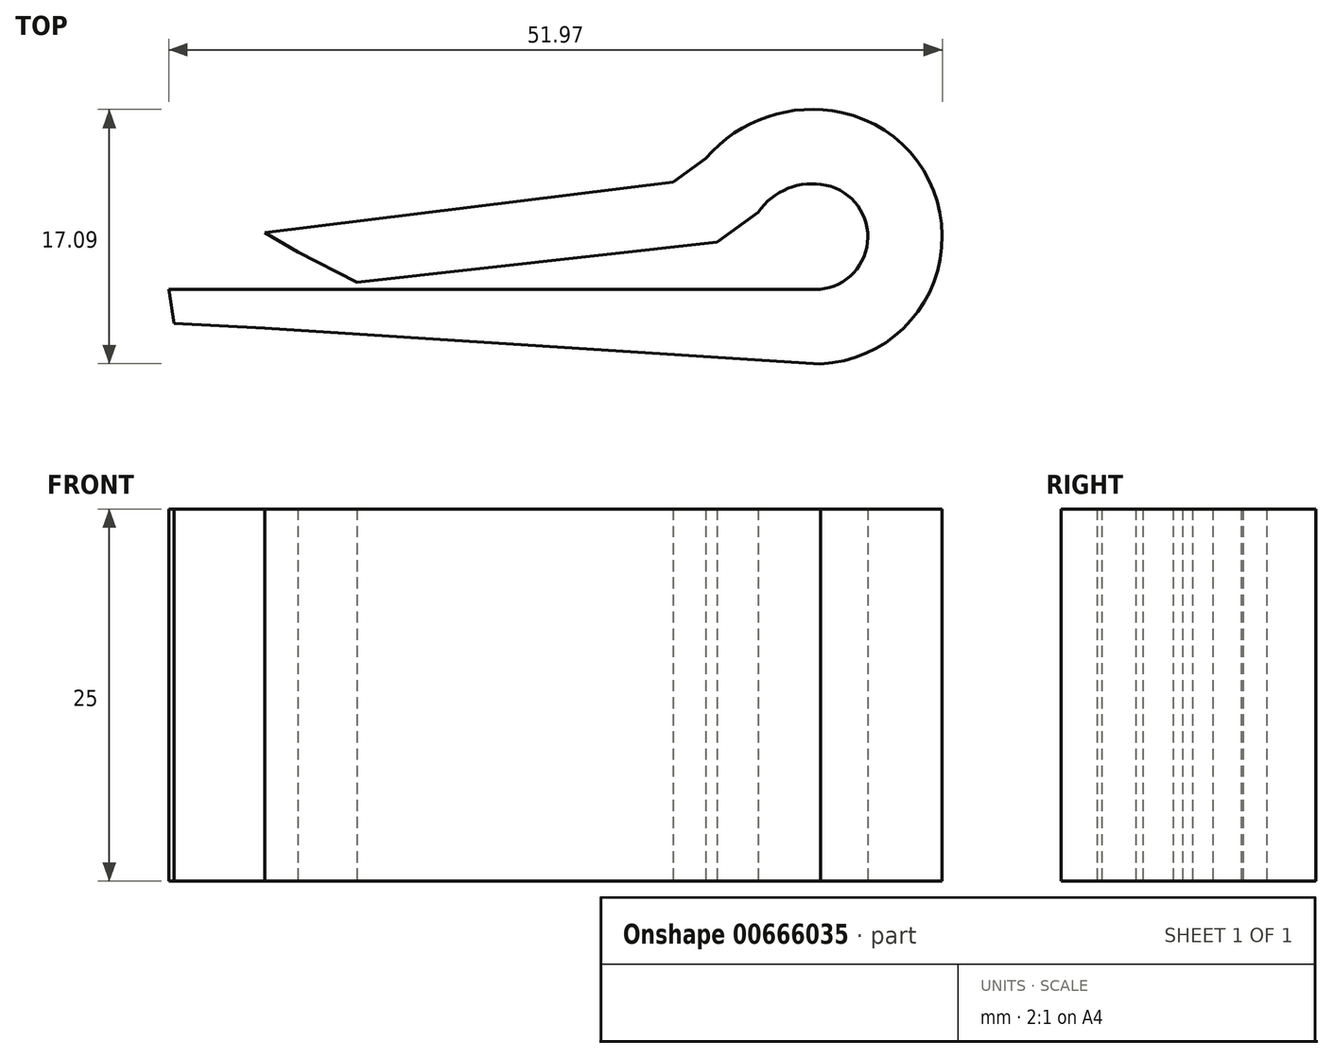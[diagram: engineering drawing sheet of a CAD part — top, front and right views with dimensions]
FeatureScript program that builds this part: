
annotation { "Feature Type Name" : "Feature", "Feature Type Description" : "" }
export const myFeature = defineFeature(function(context is Context, id is Id, definition is map)
    precondition{}
    {
        {
            var Q0;
            Q0=qCreatedBy(makeId("Top.planeOp"),FACE);
            var sketch = newSketch(context, id + "F0", { "sketchPlane" : qUnion([Q0])});
            skLineSegment(sketch, "E0", {"start": v(-26.38, -4.37) * mm, "end": v(13.62, -4.37) * mm});
            skArc(sketch, "E1", {"start": v(13.62, -4.37) * mm, "mid": v(17.15, -1.2) * mm, "end": v(14.37, 2.63) * mm});
            skArc(sketch, "E2", {"start": v(14.37, 2.63) * mm, "mid": v(11.8, 2.42) * mm, "end": v(9.8, 0.82) * mm});
            skLineSegment(sketch, "E3", {"start": v(9.8, 0.82) * mm, "end": v(7.04, -1.2) * mm});
            skLineSegment(sketch, "E4", {"start": v(7.04, -1.2) * mm, "end": v(-17.14, -3.87) * mm});
            skLineSegment(sketch, "E5", {"start": v(-17.14, -3.87) * mm, "end": v(-21.12, -1.86) * mm});
            skLineSegment(sketch, "E6", {"start": v(-21.12, -1.86) * mm, "end": v(-23.36, -0.55) * mm});
            skLineSegment(sketch, "E7.0", {"start": v(6.29, 4.44) * mm, "end": v(4.09, 2.83) * mm});
            skArc(sketch, "E7.1", {"start": v(15.42, 7.52) * mm, "mid": v(10.43, 7.24) * mm, "end": v(6.29, 4.44) * mm});
            skArc(sketch, "E7.2", {"start": v(14, -9.36) * mm, "mid": v(22.14, -1.55) * mm, "end": v(15.42, 7.52) * mm});
            skLineSegment(sketch, "E8", {"start": v(4.09, 2.83) * mm, "end": v(-23.36, -0.55) * mm});
            skLineSegment(sketch, "E9", {"start": v(14, -9.36) * mm, "end": v(-23.36, -6.95) * mm});
            skLineSegment(sketch, "E10", {"start": v(-26.38, -4.37) * mm, "end": v(-29.8, -4.37) * mm});
            skLineSegment(sketch, "E11", {"start": v(-29.8, -4.37) * mm, "end": v(-29.45, -6.66) * mm});
            skLineSegment(sketch, "E12", {"start": v(-29.45, -6.66) * mm, "end": v(-23.36, -6.95) * mm});
            skSolve(sketch);
        }
        {
            var Q0;
            Q0=makeQuery(id+"F0.imprint","IMPRINT",FACE,{"disambiguationData":[TD([[makeQuery(id+"F0.imprint","IMPRINT",EDGE,{"derivedFrom":sQuery(id+"F0.wireOp",EDGE,"E0")}),-1.0]])]});
            extrude(context, id + "F1", {"entities" : qUnion([Q0]), "depth" : 25 * mm, "offsetDistance" : 25 * mm});
        }
    });
